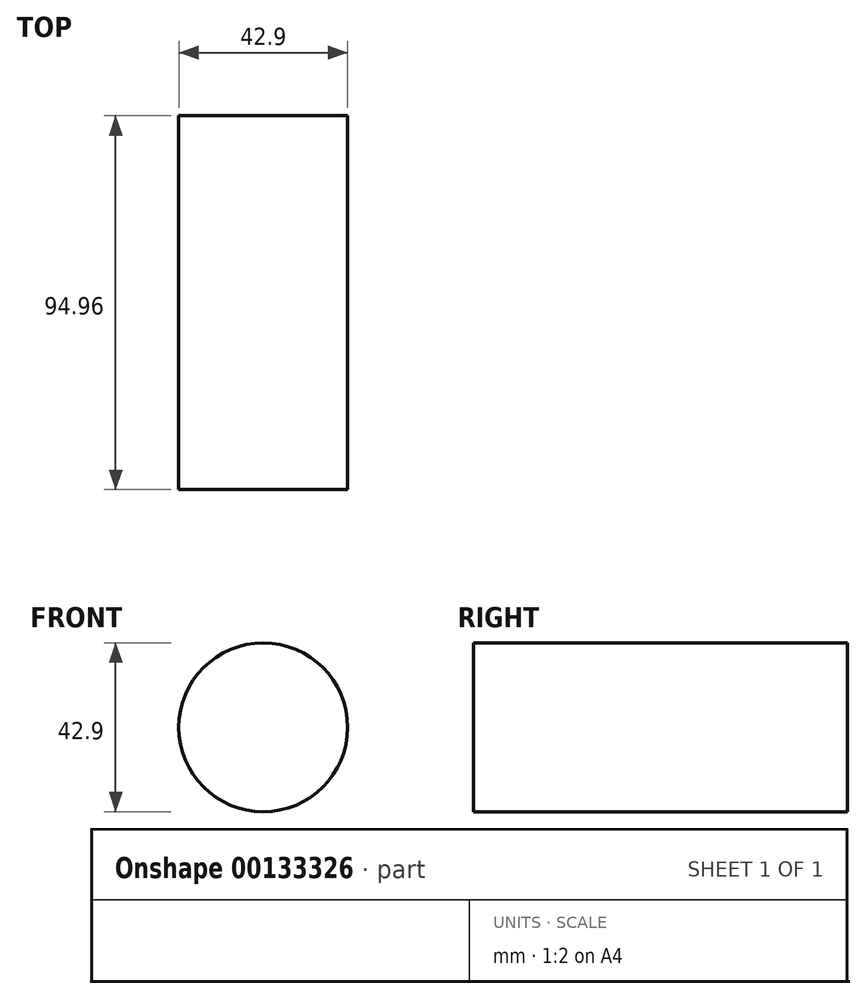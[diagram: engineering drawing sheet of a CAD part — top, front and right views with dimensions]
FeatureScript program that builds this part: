
annotation { "Feature Type Name" : "Feature", "Feature Type Description" : "" }
export const myFeature = defineFeature(function(context is Context, id is Id, definition is map)
    precondition{}
    {
        {
            var Q0;
            Q0=qCreatedBy(makeId("Front.planeOp"),FACE);
            var sketch = newSketch(context, id + "F0", { "sketchPlane" : qUnion([Q0])});
            skCircle(sketch, "E0", {"center": v(0, 0) * mm, "radius": 21.45 * mm});
            skSolve(sketch);
        }
        {
            var Q0;
            Q0=makeQuery(id+"F0.imprint","IMPRINT",FACE,{"disambiguationData":[TD([[makeQuery(id+"F0.imprint","IMPRINT",EDGE,{"derivedFrom":sQuery(id+"F0.wireOp",EDGE,"E0")}),1.0]])]});
            extrude(context, id + "F1", {"entities" : qUnion([Q0]), "depth" : 94.96 * mm});
        }
    });
